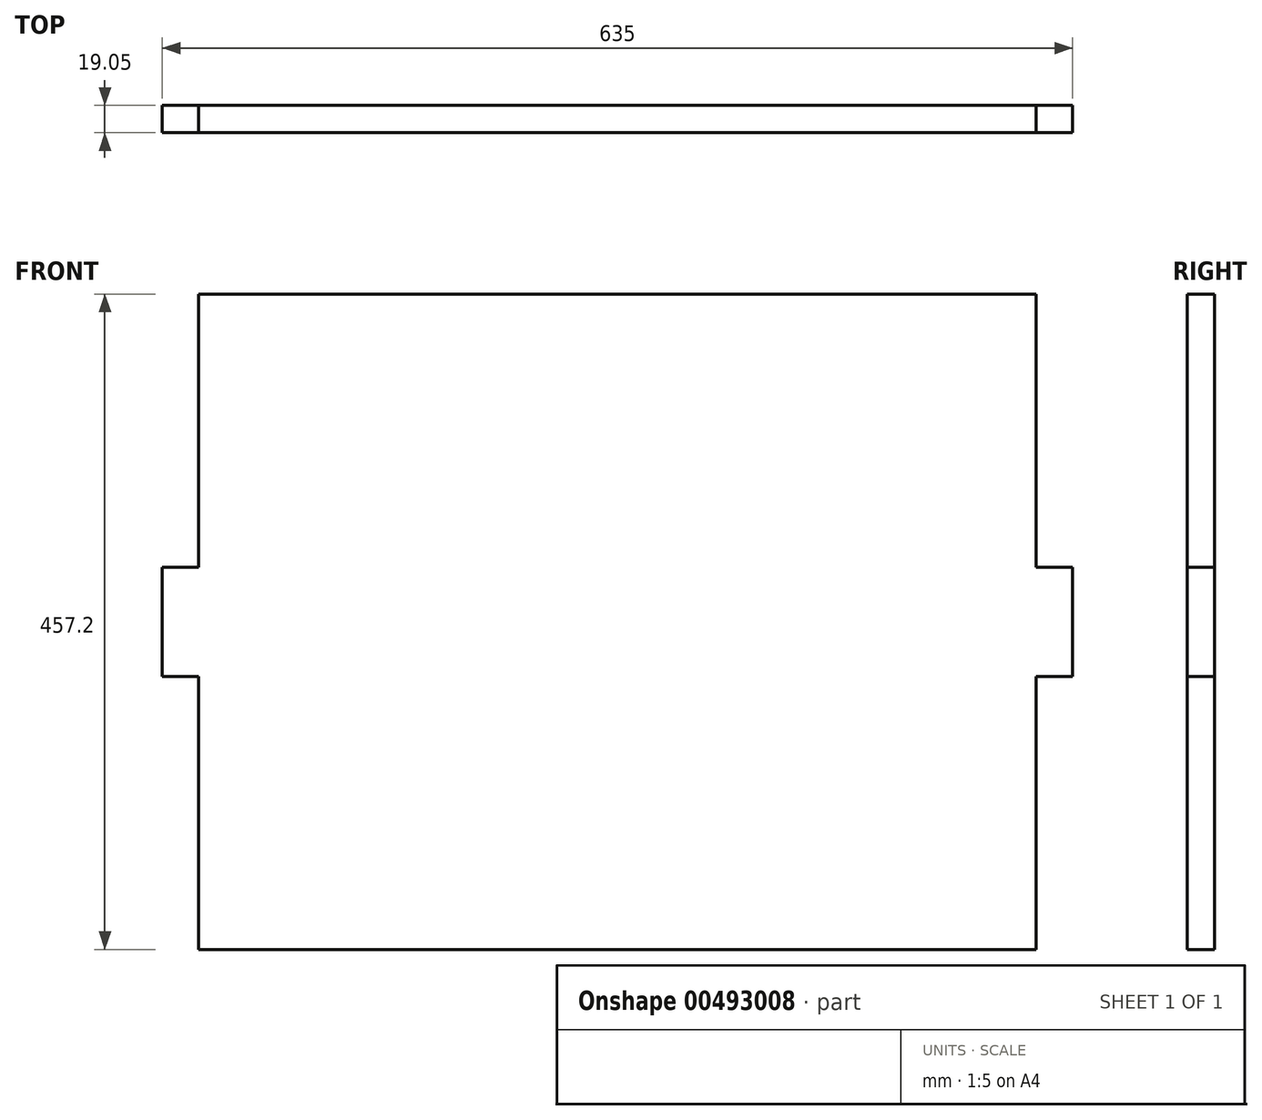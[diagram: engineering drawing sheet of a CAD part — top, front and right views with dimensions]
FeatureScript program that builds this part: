
annotation { "Feature Type Name" : "Feature", "Feature Type Description" : "" }
export const myFeature = defineFeature(function(context is Context, id is Id, definition is map)
    precondition{}
    {
        {
            var Q0;
            Q0=qCreatedBy(makeId("Front.planeOp"),FACE);
            var sketch = newSketch(context, id + "F0", { "sketchPlane" : qUnion([Q0])});
            skLineSegment(sketch, "E0.bottom", {"start": v(-380.29, 97.62) * mm, "end": v(203.91, 97.62) * mm});
            skLineSegment(sketch, "E0.top", {"start": v(-380.29, -359.58) * mm, "end": v(203.91, -359.58) * mm});
            skLineSegment(sketch, "E0.left", {"start": v(-380.29, 97.62) * mm, "end": v(-380.29, -359.58) * mm});
            skLineSegment(sketch, "E0.right", {"start": v(203.91, 97.62) * mm, "end": v(203.91, -359.58) * mm});
            skLineSegment(sketch, "E1", {"start": v(229.31, -130.98) * mm, "end": v(229.31, -92.88) * mm});
            skLineSegment(sketch, "E2", {"start": v(229.31, -130.98) * mm, "end": v(229.31, -169.08) * mm});
            skLineSegment(sketch, "E3", {"start": v(-405.69, -130.98) * mm, "end": v(-405.69, -92.88) * mm});
            skLineSegment(sketch, "E4", {"start": v(-405.69, -130.98) * mm, "end": v(-405.69, -169.08) * mm});
            skLineSegment(sketch, "E5", {"start": v(-405.69, -92.88) * mm, "end": v(-380.29, -92.88) * mm});
            skLineSegment(sketch, "E6", {"start": v(-405.69, -169.08) * mm, "end": v(-380.29, -169.08) * mm});
            skLineSegment(sketch, "E7", {"start": v(229.31, -92.88) * mm, "end": v(203.91, -92.88) * mm});
            skLineSegment(sketch, "E8", {"start": v(229.31, -169.08) * mm, "end": v(203.91, -169.08) * mm});
            skSolve(sketch);
        }
        {
            var Q0;
            Q0 = qSketchRegion(id + "F0", true);
            extrude(context, id + "F1", {"entities" : qUnion([Q0]), "depth" : 19.05 * mm, "offsetDistance" : 25.4 * mm});
        }
    });
